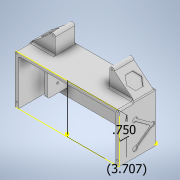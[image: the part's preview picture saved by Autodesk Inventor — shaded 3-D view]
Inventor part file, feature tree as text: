
AUTODESK INVENTOR PART (.ipt)
format: ipt  version: 2022 (Build 260153000, 153)  size: 504,832 bytes
history: native  units: in
note: dims shown in document units (in); Inventor stores cm internally (conversion verified against a paired STEP export)
features: sketch x20, extrude x16, projected_geometry x10, fillet x4, mirror x1
ambient origin geometry x8: Origin, YZ Plane, XZ Plane, XY Plane, X Axis, Y Axis, Z Axis, Center Point
bodies: Solid1 (feature_tree)
feature tree (51):
  extrude  "Extrusion1"  Depth=3.3in
  extrude  "Extrusion2"  Depth=0.125in TaperAngle=0.0deg
  extrude  "Extrusion3"  Depth=0.25in
  extrude  "Extrusion4"  Depth=1.0in
  extrude  "Extrusion5"  Depth=1.0in
  sketch  "Sketch6"  dims[d12=0.12in d13=0.12in]
  extrude  "Extrusion6"  Depth=0.12in
  extrude  "Extrusion7"  Depth=0.75in TaperAngle=0.0deg
  fillet  "Fillet1"  Radius=0.12in
  fillet  "Fillet2"  Radius=0.12in
  extrude  "Extrusion8"  Depth=0.375in
  extrude  "Extrusion9"  Depth=0.75in TaperAngle=0.0deg
  mirror  "Mirror1"
  fillet  "Fillet3"  Radius=1.25in
  extrude  "Extrusion10"  Depth=0.35in
  extrude  "Extrusion11"  Depth=1.6014in TaperAngle=0.0deg
  extrude  "Extrusion12"  Depth=0.12in
  fillet  "Fillet4"  Radius=0.125in
  sketch  "Sketch15"  dims[d30=0.12in d31=0.12in d32=0.125in d33=0.0in]
  sketch  "Sketch16"  dims[d34=3.175in d35=0.0in d36=0.125in]
  extrude  "Extrusion13"  Depth=0.125in
  extrude  "Extrusion14"  Depth=0.35in
  sketch  "Sketch18"  dims[d39=0.35in d40=0.0875in]
  sketch  "Sketch19"  dims[d42=0.045in d43=0.0in d45=0.0625in d46=0.0in]
  extrude  "Extrusion15"  Depth=0.0875in
  sketch  "Sketch21"  dims[d48=0.25in]
  sketch  "Sketch22"  dims[d49=0.125in]
  extrude  "Extrusion16"  Depth=0.0625in TaperAngle=0.0deg
  sketch  "Sketch1"  dims[d0=7.4in d1=3.3in]
  sketch  "Sketch2"  dims[d2=0.25in d3=0.125in d4=0.0in]
  projected_geometry  "Projected Loop1"
  sketch  "Sketch3"  dims[d5=1.75in d6=0.0in d7=0.25in]
  projected_geometry  "Projected Loop2"
  sketch  "Sketch4"  dims[d8=1.0in d9=0.25in]
  projected_geometry  "Projected Loop3"
  sketch  "Sketch5"  dims[d10=1.0in d11=0.12in]
  projected_geometry  "Projected Loop4"
  sketch  "Sketch7"  dims[d14=0.12in d15=0.75in d16=0.0in d17=0.12in d18=0.12in]
  projected_geometry  "Projected Loop5"
  sketch  "Sketch8"  dims[d19=0.12in d20=0.375in]
  projected_geometry  "Projected Loop6"
  sketch  "Sketch11"  dims[d21=0.12in d22=0.75in d23=0.0in d24=1.25in]
  projected_geometry  "Projected Loop7"
  sketch  "Sketch13"  dims[d25=4.5in d26=0.35in]
  sketch  "Sketch14"  dims[d27=0.35in d28=1.6014in d29=0.0in]
  projected_geometry  "Projected Loop8"
  sketch  "Sketch17"  dims[d37=0.125in d38=0.35in]
  projected_geometry  "Projected Loop9"
  sketch  "Sketch20"  dims[d47=0.25in]
  sketch  "Sketch23"  dims[d50=0.84in d51=2.85in d52=0.225in d53=1.5in d54=0.0in d56=0.1575in d57=0.3in d58=0.0in d66=0.1181in d67=0.1181in d68=0.1181in d72=0.1181in d73=0.1181in d74=0.1181in d75=0.1181in d78=0.35in d79=0.1181in d80=0.1181in d81=0.1181in d82=0.1181in d83=0.1181in d84=0.0in d85=0.125in d86=0.9in d87=0.0in d88=0.1575in d89=0.0in d90=3.7075in d91=0.375in d92=0.1181in d93=0.375in d94=0.1181in d95=1.0in d96=0.0in d97=0.75in d98=0.1181in d99=0.1181in d100=0.1181in d101=0.1181in d102=1.0in d103=0.0in]
  projected_geometry  "Projected Loop10"
